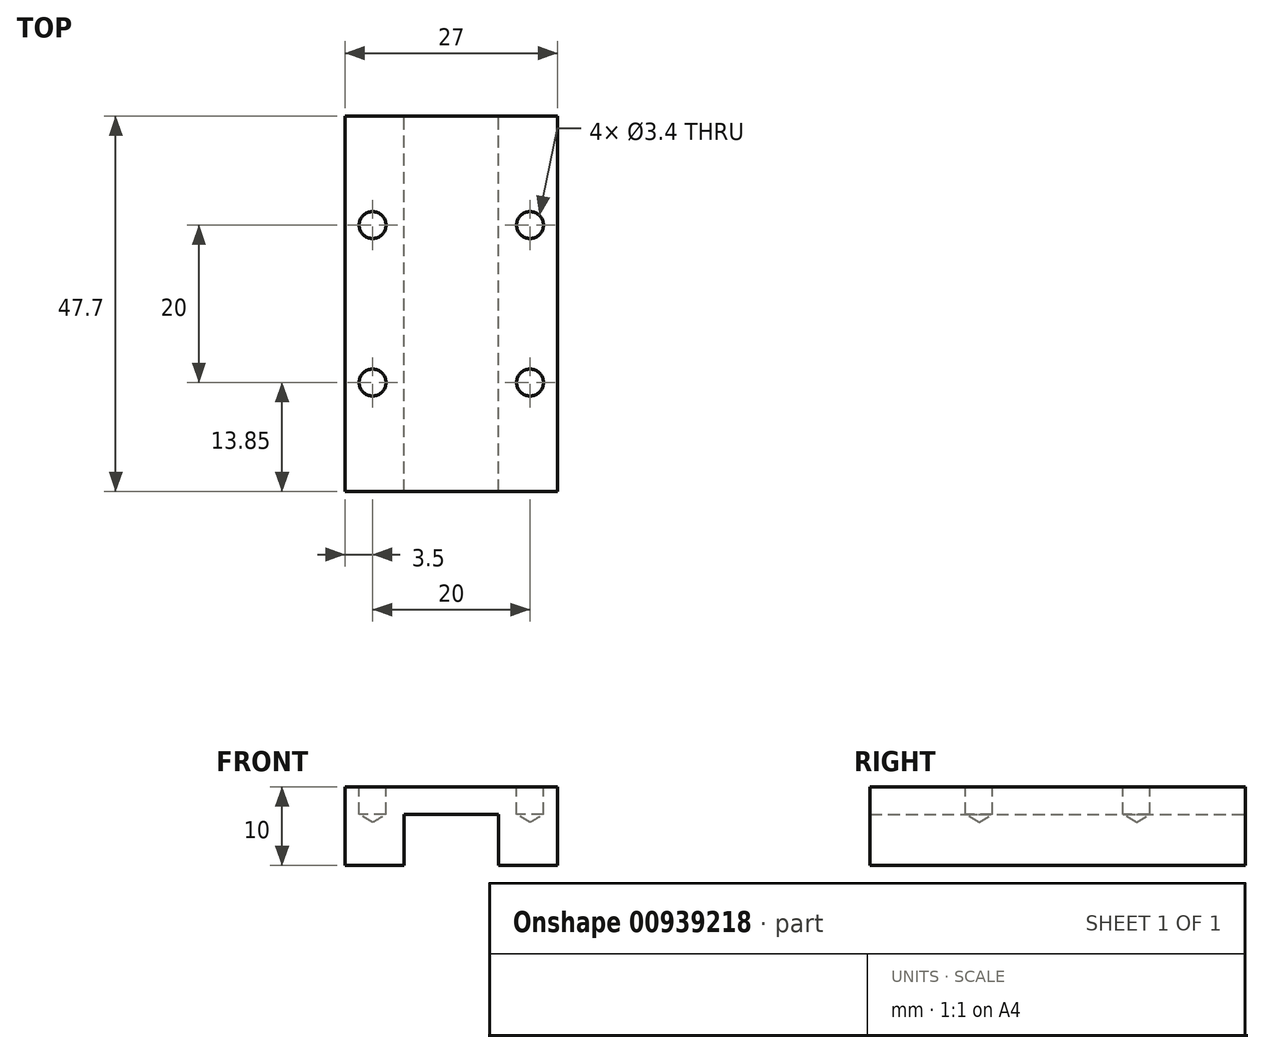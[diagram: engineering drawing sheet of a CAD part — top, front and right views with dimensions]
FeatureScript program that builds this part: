
annotation { "Feature Type Name" : "Feature", "Feature Type Description" : "" }
export const myFeature = defineFeature(function(context is Context, id is Id, definition is map)
    precondition{}
    {
        {
            var Q0;
            Q0=qCreatedBy(makeId("Front.planeOp"),FACE);
            var sketch = newSketch(context, id + "F0", { "sketchPlane" : qUnion([Q0])});
            skLineSegment(sketch, "E0.bottom", {"start": v(13.5, -5) * mm, "end": v(-13.5, -5) * mm});
            skLineSegment(sketch, "E0.top", {"start": v(13.5, 5) * mm, "end": v(-13.5, 5) * mm});
            skLineSegment(sketch, "E0.left", {"start": v(13.5, -5) * mm, "end": v(13.5, 5) * mm});
            skLineSegment(sketch, "E0.right", {"start": v(-13.5, -5) * mm, "end": v(-13.5, 5) * mm});
            skPoint(sketch, "E0.middle", {"position": v(0, 0) * mm});
            skLineSegment(sketch, "E1.bottom", {"start": v(6, -5) * mm, "end": v(-6, -5) * mm});
            skLineSegment(sketch, "E1.top", {"start": v(6, 1.5) * mm, "end": v(-6, 1.5) * mm});
            skLineSegment(sketch, "E1.left", {"start": v(6, -5) * mm, "end": v(6, 1.5) * mm});
            skLineSegment(sketch, "E1.right", {"start": v(-6, -5) * mm, "end": v(-6, 1.5) * mm});
            skPoint(sketch, "E1.middle", {"position": v(0, -1.75) * mm});
            skSolve(sketch);
        }
        {
            var Q0;
            Q0=makeQuery(id+"F0.imprint","IMPRINT",FACE,{"disambiguationData":[TD([[makeQuery(id+"F0.imprint","IMPRINT",EDGE,{"derivedFrom":sQuery(id+"F0.wireOp",EDGE,"E0.top")}),1.0]])]});
            extrude(context, id + "F1", {"entities" : qUnion([Q0]), "endBound" : BoundingType.SYMMETRIC, "depth" : 47.7 * mm, "offsetDistance" : 25 * mm});
        }
        {
            var Q0;
            Q0=makeQuery(id+"F1.opExtrude","SWEPT_FACE",FACE,{"disambiguationData":[OSD([sQuery(id+"F0.wireOp",EDGE,"E0.top")])]});
            var sketch = newSketch(context, id + "F2", { "sketchPlane" : qUnion([Q0])});
            skLineSegment(sketch, "E2.bottom", {"start": v(10, -10) * mm, "end": v(-10, -10) * mm, "construction": true});
            skLineSegment(sketch, "E2.top", {"start": v(10, 10) * mm, "end": v(-10, 10) * mm, "construction": true});
            skLineSegment(sketch, "E2.left", {"start": v(10, -10) * mm, "end": v(10, 10) * mm, "construction": true});
            skLineSegment(sketch, "E2.right", {"start": v(-10, -10) * mm, "end": v(-10, 10) * mm, "construction": true});
            skPoint(sketch, "E2.middle", {"position": v(0, 0) * mm});
            skSolve(sketch);
        }
        {
            var Q0;
            Q0=sQuery(id+"F2.wireOp",VERTEX,"E2.left.end");
            var Q1;
            Q1=sQuery(id+"F2.wireOp",VERTEX,"E2.bottom.start");
            var Q2;
            Q2=sQuery(id+"F2.wireOp",VERTEX,"E2.right.start");
            var Q3;
            Q3=sQuery(id+"F2.wireOp",VERTEX,"E2.right.end");
            var Q4;
            Q4=makeQuery(id+"F1.opExtrude","SWEPT_BODY",BODY,{"disambiguationData":[OSD([sQuery(id+"F0.wireOp",EDGE,"E0.bottom"),sQuery(id+"F0.wireOp",EDGE,"E0.top"),sQuery(id+"F0.wireOp",EDGE,"E0.left"),sQuery(id+"F0.wireOp",EDGE,"E0.right"),sQuery(id+"F0.wireOp",EDGE,"E1.top"),sQuery(id+"F0.wireOp",EDGE,"E1.left"),sQuery(id+"F0.wireOp",EDGE,"E1.right")])]});
            hole(context, id + "F3", {"style" : HoleStyle.SIMPLE, "endStyle" : HoleEndStyle.BLIND, "standardTappedOrClearance" : lookupTablePath({ "standard" : "ISO", "fit" : "Normal", "size" : "M3", "type" : "Clearance" }), "standardBlindInLast" : lookupTablePath({ "fit" : "Normal", "standard" : "ISO", "engagement" : "75%", "pitch" : "0.5 mm", "size" : "M3", "type" : "Clearance & tapped" }), "holeDiameter" : 3.4 * mm, "majorDiameter" : 5 * mm, "holeDepth" : 3.5 * mm, "isTappedThrough" : true, "tappedDepth" : 12 * mm, "tapClearance" : 3, "locations" : qUnion([Q0, Q1, Q2, Q3]), "scope" : qUnion([Q4])});
        }
    });
